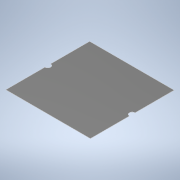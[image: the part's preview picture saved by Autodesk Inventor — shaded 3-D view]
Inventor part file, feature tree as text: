
AUTODESK INVENTOR PART (.ipt)
format: ipt  version: 2022 (Build 260153000, 153)  size: 110,592 bytes
history: native  units: in
note: dims shown in document units (in); Inventor stores cm internally (conversion verified against a paired STEP export)
features: extrude x2, sketch x2
ambient origin geometry x8: Origin, YZ Plane, XZ Plane, XY Plane, X Axis, Y Axis, Z Axis, Center Point
bodies: Solid1 (feature_tree)
feature tree (4):
  extrude  "Extrusion1"  Depth=1.7087in
  extrude  "Extrusion2"  Depth=0.0591in
  sketch  "Sketch1"  dims[d0=1.6929in d1=1.7087in]
  sketch  "Sketch2"  dims[d2=0.0031in d3=0.0in d5=0.0591in d6=0.0in d7=0.0in]
